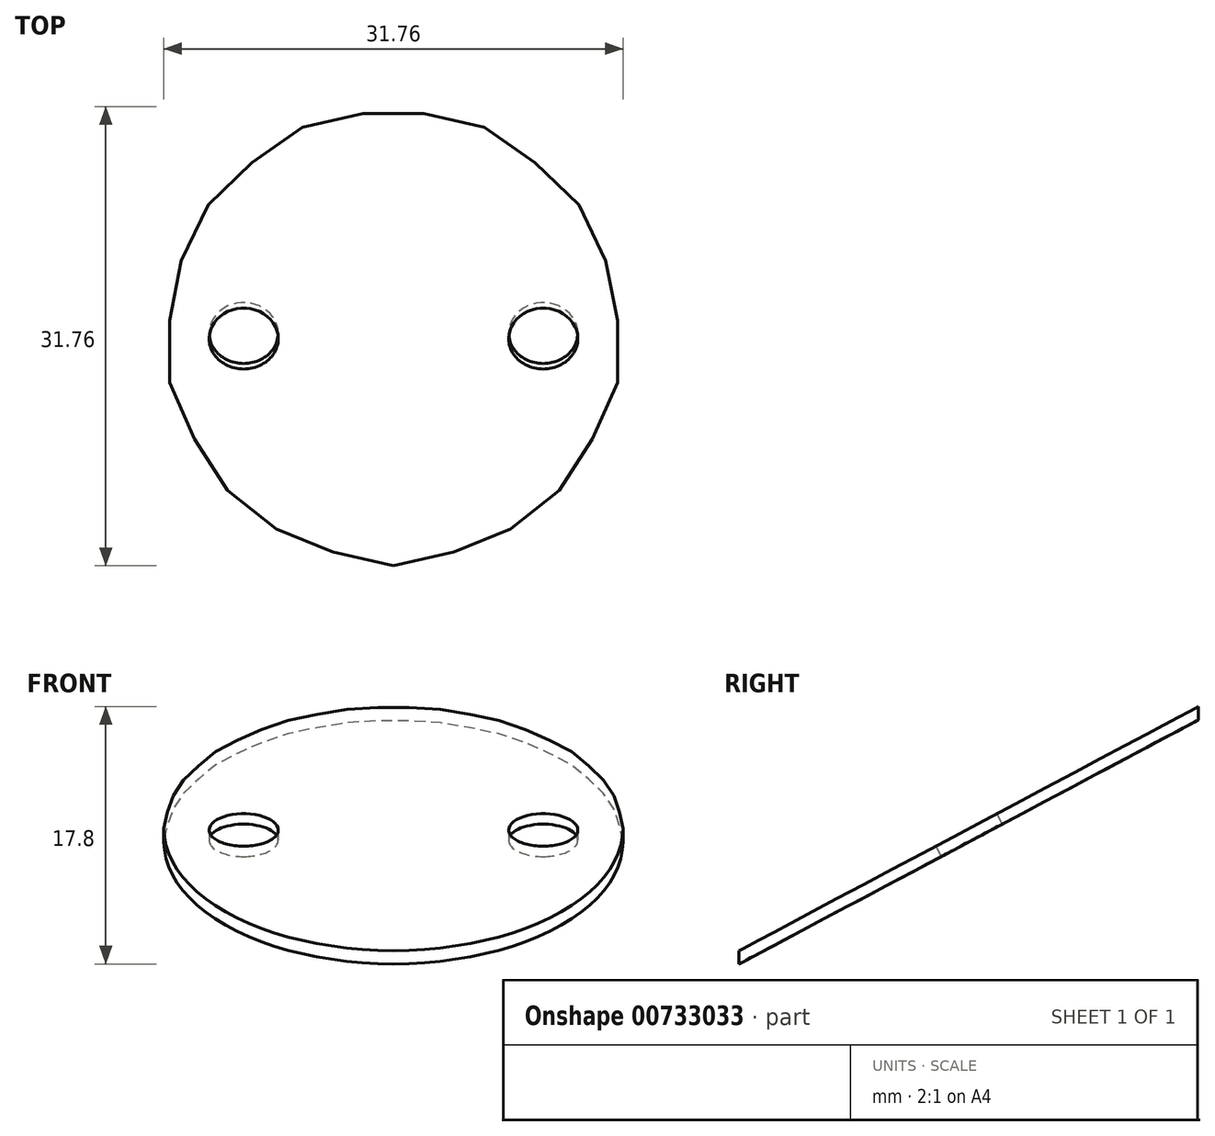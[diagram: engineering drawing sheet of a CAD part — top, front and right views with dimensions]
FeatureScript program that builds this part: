
annotation { "Feature Type Name" : "Feature", "Feature Type Description" : "" }
export const myFeature = defineFeature(function(context is Context, id is Id, definition is map)
    precondition{}
    {
        {
            var Q0;
            Q0=qCreatedBy(makeId("Top.planeOp"),FACE);
            var sketch = newSketch(context, id + "F0", { "sketchPlane" : qUnion([Q0])});
            skCircle(sketch, "E0", {"center": v(0, 0) * mm, "radius": 15.88 * mm});
            skSolve(sketch);
        }
        {
            var Q0;
            Q0 = qSketchRegion(id + "F0", true);
            extrude(context, id + "F1", {"entities" : qUnion([Q0]), "depth" : 25.4 * mm, "offsetDistance" : 25.4 * mm});
        }
        {
            var Q0;
            Q0=qCreatedBy(makeId("Front.planeOp"),FACE);
            var sketch = newSketch(context, id + "F2", { "sketchPlane" : qUnion([Q0])});
            skLineSegment(sketch, "E1.bottom", {"start": v(30.19, -12.7) * mm, "end": v(-30.19, -12.7) * mm});
            skLineSegment(sketch, "E1.top", {"start": v(30.19, 12.7) * mm, "end": v(-30.19, 12.7) * mm});
            skLineSegment(sketch, "E1.left", {"start": v(30.19, -12.7) * mm, "end": v(30.19, 12.7) * mm});
            skLineSegment(sketch, "E1.right", {"start": v(-30.19, -12.7) * mm, "end": v(-30.19, 12.7) * mm});
            skPoint(sketch, "E1.middle", {"position": v(0, 0) * mm});
            skSolve(sketch);
        }
        {
            var Q0;
            Q0=sQuery(id+"F2.wireOp",EDGE,"E1.top");
            cPlane(context, id + "F3", {"entities" : qUnion([Q0]), "cplaneType" : CPlaneType.LINE_ANGLE, "offset" : 25.4 * mm, "angle" : 62 * degree, "width" : 152.4 * mm, "height" : 152.4 * mm});
        }
        {
            var Q0;
            Q0=qCreatedBy(id+"F3.planeOp",FACE);
            cPlane(context, id + "F4", {"entities" : qUnion([Q0]), "cplaneType" : CPlaneType.OFFSET, "offset" : 0.81 * mm, "width" : 152.4 * mm, "height" : 152.4 * mm});
        }
        {
            var Q0;
            Q0=qCreatedBy(id+"F4.planeOp",FACE);
            var sketch = newSketch(context, id + "F5", { "sketchPlane" : qUnion([Q0])});
            skCircle(sketch, "E2", {"center": v(0, 0) * mm, "radius": 28 * mm});
            skSolve(sketch);
        }
        {
            var Q0;
            Q0 = qSketchRegion(id + "F5", true);
            extrude(context, id + "F6", {"entities" : qUnion([Q0]), "operationType" : NewBodyOperationType.REMOVE, "depth" : 25.4 * mm, "offsetDistance" : 25.4 * mm});
        }
        {
            var Q0;
            Q0=qCreatedBy(id+"F3.planeOp",FACE);
            var sketch = newSketch(context, id + "F7", { "sketchPlane" : qUnion([Q0])});
            skCircle(sketch, "E3", {"center": v(-3.1, 4.32) * mm, "radius": 26.72 * mm});
            skSolve(sketch);
        }
        {
            var Q0;
            Q0 = qSketchRegion(id + "F7", true);
            extrude(context, id + "F8", {"entities" : qUnion([Q0]), "operationType" : NewBodyOperationType.REMOVE, "oppositeDirection" : true, "depth" : 25.4 * mm, "offsetDistance" : 25.4 * mm});
        }
        {
            var Q0;
            Q0=qCreatedBy(id+"F3.planeOp",FACE);
            var sketch = newSketch(context, id + "F9", { "sketchPlane" : qUnion([Q0])});
            skCircle(sketch, "E4", {"center": v(-10.35, 6.2) * mm, "radius": 2.39 * mm});
            skCircle(sketch, "E5", {"center": v(10.35, 6.2) * mm, "radius": 2.39 * mm});
            skSolve(sketch);
        }
        {
            var Q0;
            Q0 = qSketchRegion(id + "F9", true);
            extrude(context, id + "F10", {"entities" : qUnion([Q0]), "operationType" : NewBodyOperationType.REMOVE, "depth" : 25.4 * mm, "offsetDistance" : 25.4 * mm});
        }
    });
